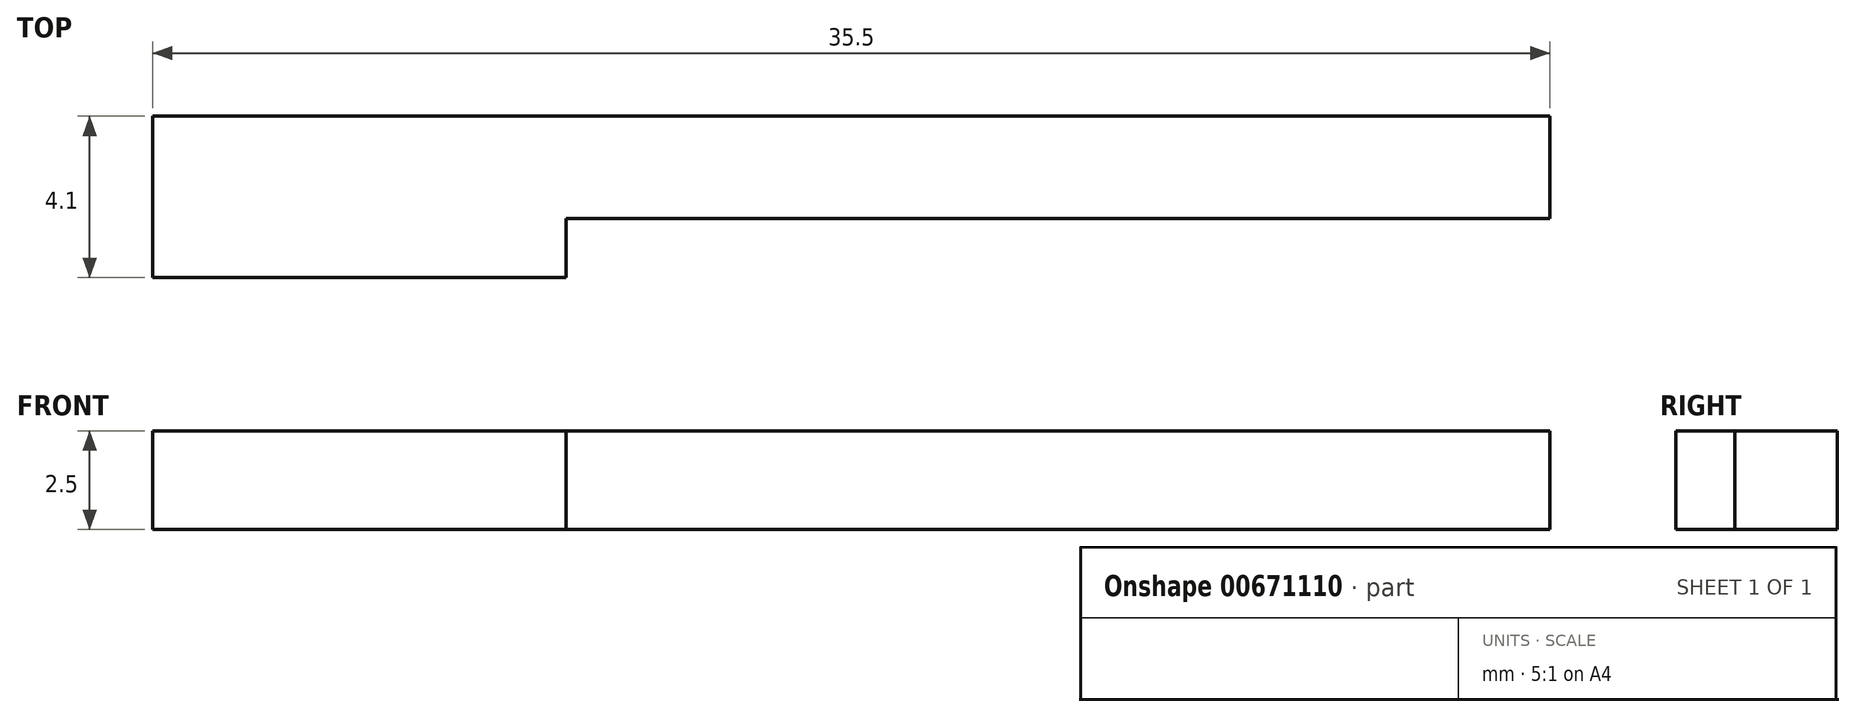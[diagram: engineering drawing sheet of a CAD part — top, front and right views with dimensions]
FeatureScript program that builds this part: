
annotation { "Feature Type Name" : "Feature", "Feature Type Description" : "" }
export const myFeature = defineFeature(function(context is Context, id is Id, definition is map)
    precondition{}
    {
        {
            var Q0;
            Q0=qCreatedBy(makeId("Top.planeOp"),FACE);
            var sketch = newSketch(context, id + "F0", { "sketchPlane" : qUnion([Q0])});
            skLineSegment(sketch, "E0.bottom", {"start": v(-31.6, 39.17) * mm, "end": v(-42.1, 39.17) * mm});
            skLineSegment(sketch, "E0.top", {"start": v(-31.6, 35.07) * mm, "end": v(-42.1, 35.07) * mm});
            skLineSegment(sketch, "E0.left", {"start": v(-31.6, 39.17) * mm, "end": v(-31.6, 35.07) * mm});
            skLineSegment(sketch, "E0.right", {"start": v(-42.1, 39.17) * mm, "end": v(-42.1, 35.07) * mm});
            skPoint(sketch, "E0.middle", {"position": v(-36.85, 37.12) * mm});
            skLineSegment(sketch, "E1.bottom", {"start": v(-31.6, 39.17) * mm, "end": v(-6.6, 39.17) * mm});
            skLineSegment(sketch, "E1.top", {"start": v(-31.6, 36.57) * mm, "end": v(-6.6, 36.57) * mm});
            skLineSegment(sketch, "E1.left", {"start": v(-31.6, 39.17) * mm, "end": v(-31.6, 36.57) * mm});
            skLineSegment(sketch, "E1.right", {"start": v(-6.6, 39.17) * mm, "end": v(-6.6, 36.57) * mm});
            skSolve(sketch);
        }
        {
            var Q0;
            Q0=qSketchRegion(id+"F0",true);
            extrude(context, id + "F1", {"entities" : qUnion([Q0]), "depth" : 2.5 * mm});
        }
    });
